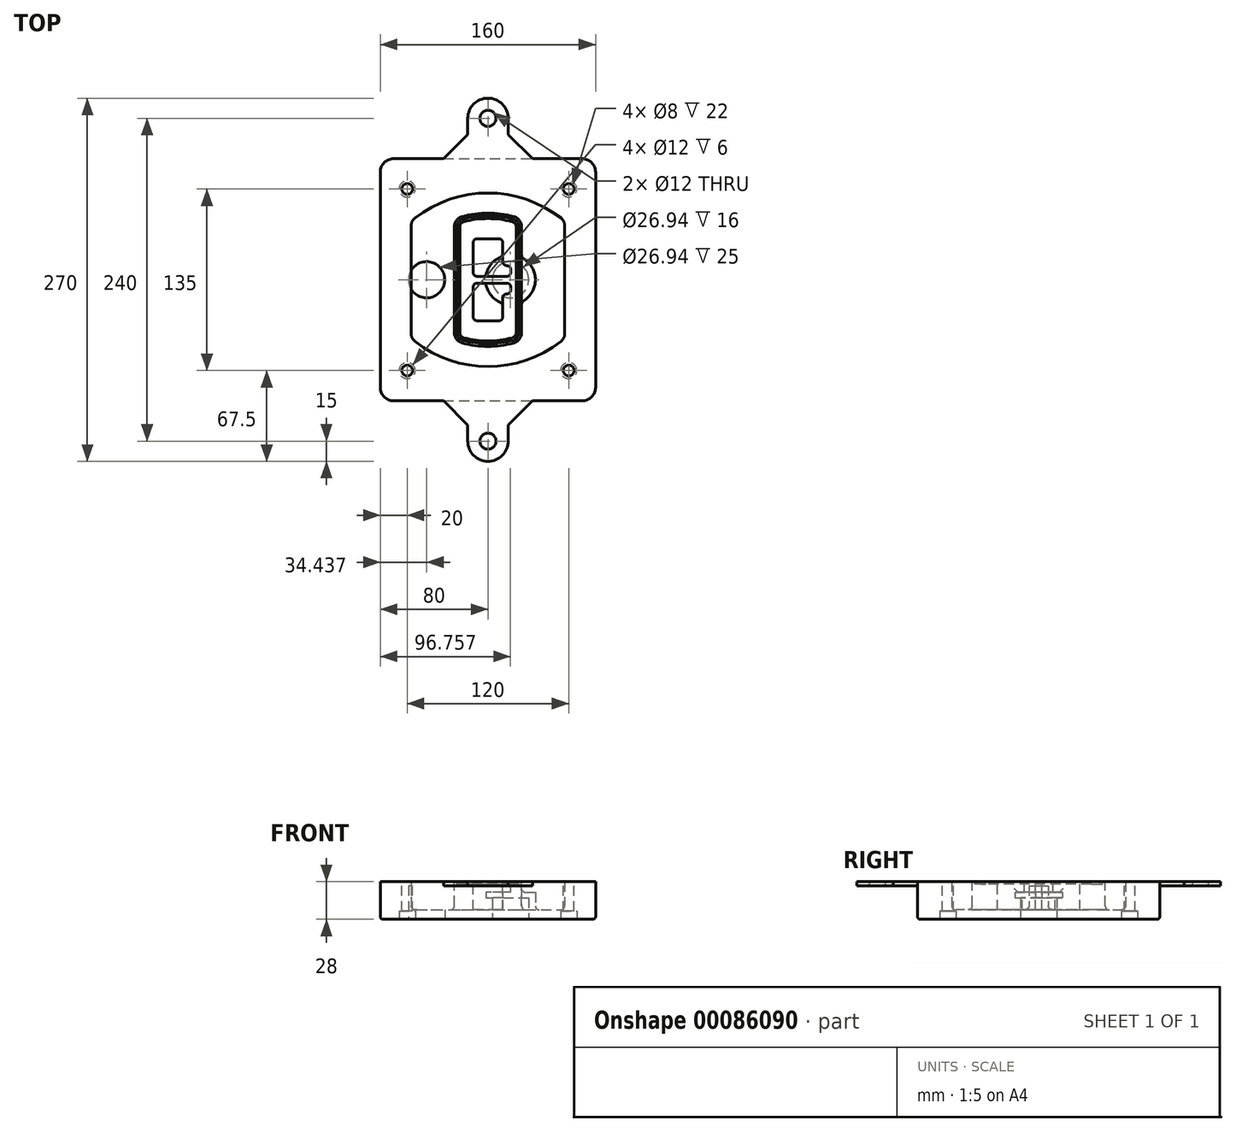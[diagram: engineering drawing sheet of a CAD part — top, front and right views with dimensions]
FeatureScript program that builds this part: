
annotation { "Feature Type Name" : "Feature", "Feature Type Description" : "" }
export const myFeature = defineFeature(function(context is Context, id is Id, definition is map)
    precondition{}
    {
        {
            var Q0;
            Q0=qCreatedBy(makeId("Top.planeOp"),FACE);
            var sketch = newSketch(context, id + "F0", { "sketchPlane" : qUnion([Q0])});
            skPoint(sketch, "E0.rect.middle", {"position": v(0, 0) * mm});
            skLineSegment(sketch, "E1.bottom", {"start": v(-70, -90) * mm, "end": v(70, -90) * mm});
            skLineSegment(sketch, "E1.top", {"start": v(-70, 90) * mm, "end": v(70, 90) * mm});
            skLineSegment(sketch, "E1.left", {"start": v(-80, -80) * mm, "end": v(-80, 80) * mm});
            skLineSegment(sketch, "E1.right", {"start": v(80, -80) * mm, "end": v(80, 80) * mm});
            skLineSegment(sketch, "E2", {"start": v(-80, 90) * mm, "end": v(80, -90) * mm, "construction": true});
            skLineSegment(sketch, "E3", {"start": v(80, 90) * mm, "end": v(-80, -90) * mm, "construction": true});
            skCircle(sketch, "E4", {"center": v(-60, 67.5) * mm, "radius": 4 * mm});
            skCircle(sketch, "E5", {"center": v(60, 67.5) * mm, "radius": 4 * mm});
            skCircle(sketch, "E6", {"center": v(60, -67.5) * mm, "radius": 4 * mm});
            skCircle(sketch, "E7", {"center": v(-60, -67.5) * mm, "radius": 4 * mm});
            skLineSegment(sketch, "E8", {"start": v(-60, 67.5) * mm, "end": v(60, 67.5) * mm, "construction": true});
            skLineSegment(sketch, "E9", {"start": v(60, 67.5) * mm, "end": v(60, -67.5) * mm, "construction": true});
            skLineSegment(sketch, "E10", {"start": v(60, -67.5) * mm, "end": v(-60, -67.5) * mm, "construction": true});
            skLineSegment(sketch, "E11", {"start": v(-60, -67.5) * mm, "end": v(-60, 67.5) * mm, "construction": true});
            skLineSegment(sketch, "E12", {"start": v(-60, 40.3) * mm, "end": v(-60, -40.3) * mm});
            skLineSegment(sketch, "E13", {"start": v(60, 40.3) * mm, "end": v(60, -40.3) * mm});
            skArc(sketch, "E14", {"start": v(56.15, 48.18) * mm, "mid": v(0, 67.5) * mm, "end": v(-56.15, 48.18) * mm});
            skArc(sketch, "E15", {"start": v(-56.15, -48.18) * mm, "mid": v(0, -67.5) * mm, "end": v(56.15, -48.18) * mm});
            skLineSegment(sketch, "E16", {"start": v(-60, 0) * mm, "end": v(60, 0) * mm, "construction": true});
            skPoint(sketch, "E17.visualSharp", {"position": v(-60, -45) * mm});
            skArc(sketch, "E17.filletArc", {"start": v(-60, -40.3) * mm, "mid": v(-58.99, -44.68) * mm, "end": v(-56.15, -48.18) * mm});
            skPoint(sketch, "E18.visualSharp", {"position": v(-60, 45) * mm});
            skArc(sketch, "E18.filletArc", {"start": v(-56.15, 48.18) * mm, "mid": v(-58.99, 44.68) * mm, "end": v(-60, 40.3) * mm});
            skPoint(sketch, "E19.visualSharp", {"position": v(60, 45) * mm});
            skArc(sketch, "E19.filletArc", {"start": v(60, 40.3) * mm, "mid": v(58.99, 44.68) * mm, "end": v(56.15, 48.18) * mm});
            skPoint(sketch, "E20.visualSharp", {"position": v(60, -45) * mm});
            skArc(sketch, "E20.filletArc", {"start": v(56.15, -48.18) * mm, "mid": v(58.99, -44.68) * mm, "end": v(60, -40.3) * mm});
            skPoint(sketch, "E21.visualSharp", {"position": v(-80, 90) * mm});
            skArc(sketch, "E21.filletArc", {"start": v(-70, 90) * mm, "mid": v(-77.07, 87.07) * mm, "end": v(-80, 80) * mm});
            skPoint(sketch, "E22.visualSharp", {"position": v(80, 90) * mm});
            skArc(sketch, "E22.filletArc", {"start": v(80, 80) * mm, "mid": v(77.07, 87.07) * mm, "end": v(70, 90) * mm});
            skPoint(sketch, "E23.visualSharp", {"position": v(80, -90) * mm});
            skArc(sketch, "E23.filletArc", {"start": v(70, -90) * mm, "mid": v(77.07, -87.07) * mm, "end": v(80, -80) * mm});
            skPoint(sketch, "E24.visualSharp", {"position": v(-80, -90) * mm});
            skArc(sketch, "E24.filletArc", {"start": v(-80, -80) * mm, "mid": v(-77.07, -87.07) * mm, "end": v(-70, -90) * mm});
            skArc(sketch, "E25.0", {"start": v(57, 40.3) * mm, "mid": v(56.3, 43.36) * mm, "end": v(54.3, 45.81) * mm});
            skLineSegment(sketch, "E25.1", {"start": v(57, 40.3) * mm, "end": v(57, -40.3) * mm});
            skArc(sketch, "E25.2", {"start": v(54.3, -45.81) * mm, "mid": v(56.3, -43.36) * mm, "end": v(57, -40.3) * mm});
            skArc(sketch, "E25.3", {"start": v(-54.3, -45.81) * mm, "mid": v(0, -64.5) * mm, "end": v(54.3, -45.81) * mm});
            skArc(sketch, "E25.4", {"start": v(-57, -40.3) * mm, "mid": v(-56.3, -43.36) * mm, "end": v(-54.3, -45.81) * mm});
            skArc(sketch, "E25.5", {"start": v(54.3, 45.81) * mm, "mid": v(0, 64.5) * mm, "end": v(-54.3, 45.81) * mm});
            skLineSegment(sketch, "E25.6", {"start": v(-57, 40.3) * mm, "end": v(-57, -40.3) * mm});
            skArc(sketch, "E25.7", {"start": v(-54.3, 45.81) * mm, "mid": v(-56.3, 43.36) * mm, "end": v(-57, 40.3) * mm});
            skArc(sketch, "E26.0", {"start": v(-58.62, 51.33) * mm, "mid": v(-62.58, 46.43) * mm, "end": v(-64, 40.3) * mm});
            skArc(sketch, "E26.1", {"start": v(58.62, 51.33) * mm, "mid": v(0, 71.5) * mm, "end": v(-58.62, 51.33) * mm});
            skArc(sketch, "E26.2", {"start": v(64, 40.3) * mm, "mid": v(62.58, 46.43) * mm, "end": v(58.62, 51.33) * mm});
            skLineSegment(sketch, "E26.3", {"start": v(64, 40.3) * mm, "end": v(64, -40.3) * mm});
            skArc(sketch, "E26.4", {"start": v(58.62, -51.33) * mm, "mid": v(62.58, -46.43) * mm, "end": v(64, -40.3) * mm});
            skLineSegment(sketch, "E26.5", {"start": v(-64, 40.3) * mm, "end": v(-64, -40.3) * mm});
            skArc(sketch, "E26.6", {"start": v(-58.62, -51.33) * mm, "mid": v(0, -71.5) * mm, "end": v(58.62, -51.33) * mm});
            skArc(sketch, "E26.7", {"start": v(-64, -40.3) * mm, "mid": v(-62.58, -46.43) * mm, "end": v(-58.62, -51.33) * mm});
            skSolve(sketch);
        }
        {
            var Q0;
            Q0=makeQuery(id+"F0.imprint","IMPRINT",FACE,{"disambiguationData":[TD([[makeQuery(id+"F0.imprint","IMPRINT",EDGE,{"derivedFrom":sQuery(id+"F0.wireOp",EDGE,"E1.bottom")}),1.0]])]});
            var Q1;
            Q1=makeQuery(id+"F0.imprint","IMPRINT",FACE,{"disambiguationData":[TD([[makeQuery(id+"F0.imprint","IMPRINT",EDGE,{"derivedFrom":sQuery(id+"F0.wireOp",EDGE,"E12")}),1.0]])]});
            var Q2;
            Q2=makeQuery(id+"F0.imprint","IMPRINT",FACE,{"disambiguationData":[TD([[makeQuery(id+"F0.imprint","IMPRINT",EDGE,{"derivedFrom":sQuery(id+"F0.wireOp",EDGE,"E25.0")}),1.0]])]});
            var Q3;
            Q3=makeQuery(id+"F0.imprint","IMPRINT",FACE,{"disambiguationData":[TD([[makeQuery(id+"F0.imprint","IMPRINT",EDGE,{"derivedFrom":sQuery(id+"F0.wireOp",EDGE,"E12")}),-1.0]])]});
            extrude(context, id + "F1", {"entities" : qUnion([Q0, Q1, Q2, Q3]), "oppositeDirection" : true, "depth" : 25 * mm});
        }
        {
            var Q0;
            Q0=makeQuery(id+"F0.imprint","IMPRINT",FACE,{"disambiguationData":[TD([[makeQuery(id+"F0.imprint","IMPRINT",EDGE,{"derivedFrom":sQuery(id+"F0.wireOp",EDGE,"E12")}),1.0]])]});
            extrude(context, id + "F2", {"entities" : qUnion([Q0]), "operationType" : NewBodyOperationType.ADD, "depth" : 3 * mm});
        }
        {
            var Q0;
            Q0=makeQuery(id+"F0.imprint","IMPRINT",FACE,{"disambiguationData":[TD([[makeQuery(id+"F0.imprint","IMPRINT",EDGE,{"derivedFrom":sQuery(id+"F0.wireOp",EDGE,"E25.0")}),1.0]])]});
            extrude(context, id + "F3", {"entities" : qUnion([Q0]), "operationType" : NewBodyOperationType.REMOVE, "oppositeDirection" : true, "depth" : 18 * mm});
        }
        {
            var Q0;
            Q0=makeQuery(id+"F2.opExtrude","CAP_FACE",FACE,{"disambiguationData":[OSD([sQuery(id+"F0.wireOp",EDGE,"E12"),sQuery(id+"F0.wireOp",EDGE,"E13"),sQuery(id+"F0.wireOp",EDGE,"E14"),sQuery(id+"F0.wireOp",EDGE,"E15"),sQuery(id+"F0.wireOp",EDGE,"E17.filletArc"),sQuery(id+"F0.wireOp",EDGE,"E18.filletArc"),sQuery(id+"F0.wireOp",EDGE,"E19.filletArc"),sQuery(id+"F0.wireOp",EDGE,"E20.filletArc"),sQuery(id+"F0.wireOp",EDGE,"E25.0"),sQuery(id+"F0.wireOp",EDGE,"E25.1"),sQuery(id+"F0.wireOp",EDGE,"E25.2"),sQuery(id+"F0.wireOp",EDGE,"E25.3"),sQuery(id+"F0.wireOp",EDGE,"E25.4"),sQuery(id+"F0.wireOp",EDGE,"E25.5"),sQuery(id+"F0.wireOp",EDGE,"E25.6"),sQuery(id+"F0.wireOp",EDGE,"E25.7")])],"isStart":false});
            var sketch = newSketch(context, id + "F4", { "sketchPlane" : qUnion([Q0])});
            skArc(sketch, "E27.0", {"start": v(-19.08, -46.97) * mm, "mid": v(0, -49.5) * mm, "end": v(19.08, -46.97) * mm});
            skArc(sketch, "E28.0", {"start": v(19.08, 46.97) * mm, "mid": v(0, 49.5) * mm, "end": v(-19.08, 46.97) * mm});
            skLineSegment(sketch, "E29", {"start": v(-25, 39.25) * mm, "end": v(-25, -39.25) * mm});
            skLineSegment(sketch, "E30", {"start": v(25, 39.25) * mm, "end": v(25, -39.25) * mm});
            skLineSegment(sketch, "E31", {"start": v(-25, 45.1) * mm, "end": v(25, 45.1) * mm, "construction": true});
            skLineSegment(sketch, "E32", {"start": v(-25, -45.1) * mm, "end": v(25, -45.1) * mm, "construction": true});
            skPoint(sketch, "E33.visualSharp", {"position": v(-25, 45.1) * mm});
            skArc(sketch, "E33.filletArc", {"start": v(-19.08, 46.97) * mm, "mid": v(-23.35, 44.11) * mm, "end": v(-25, 39.25) * mm});
            skPoint(sketch, "E34.visualSharp", {"position": v(25, 45.1) * mm});
            skArc(sketch, "E34.filletArc", {"start": v(25, 39.25) * mm, "mid": v(23.35, 44.11) * mm, "end": v(19.08, 46.97) * mm});
            skPoint(sketch, "E35.visualSharp", {"position": v(25, -45.1) * mm});
            skArc(sketch, "E35.filletArc", {"start": v(19.08, -46.97) * mm, "mid": v(23.35, -44.11) * mm, "end": v(25, -39.25) * mm});
            skPoint(sketch, "E36.visualSharp", {"position": v(-25, -45.1) * mm});
            skArc(sketch, "E36.filletArc", {"start": v(-25, -39.25) * mm, "mid": v(-23.35, -44.11) * mm, "end": v(-19.08, -46.97) * mm});
            skArc(sketch, "E37.0", {"start": v(54.3, 45.81) * mm, "mid": v(0, 64.5) * mm, "end": v(-54.3, 45.81) * mm});
            skArc(sketch, "E37.1", {"start": v(-54.3, 45.81) * mm, "mid": v(-56.3, 43.36) * mm, "end": v(-57, 40.3) * mm});
            skLineSegment(sketch, "E37.2", {"start": v(-57, 40.3) * mm, "end": v(-57, -40.3) * mm});
            skArc(sketch, "E37.3", {"start": v(-57, -40.3) * mm, "mid": v(-56.3, -43.36) * mm, "end": v(-54.3, -45.81) * mm});
            skArc(sketch, "E37.4", {"start": v(-54.3, -45.81) * mm, "mid": v(0, -64.5) * mm, "end": v(54.3, -45.81) * mm});
            skArc(sketch, "E37.5", {"start": v(54.3, -45.81) * mm, "mid": v(56.3, -43.36) * mm, "end": v(57, -40.3) * mm});
            skLineSegment(sketch, "E37.6", {"start": v(57, 40.3) * mm, "end": v(57, -40.3) * mm});
            skArc(sketch, "E37.7", {"start": v(57, 40.3) * mm, "mid": v(56.3, 43.36) * mm, "end": v(54.3, 45.81) * mm});
            skLineSegment(sketch, "E38.0", {"start": v(23, 39.25) * mm, "end": v(23, -39.25) * mm});
            skArc(sketch, "E38.1", {"start": v(18.56, -45.04) * mm, "mid": v(21.76, -42.9) * mm, "end": v(23, -39.25) * mm});
            skArc(sketch, "E38.2", {"start": v(-18.56, -45.04) * mm, "mid": v(0, -47.5) * mm, "end": v(18.56, -45.04) * mm});
            skArc(sketch, "E38.3", {"start": v(-23, -39.25) * mm, "mid": v(-21.76, -42.9) * mm, "end": v(-18.56, -45.04) * mm});
            skLineSegment(sketch, "E38.4", {"start": v(-23, 39.25) * mm, "end": v(-23, -39.25) * mm});
            skArc(sketch, "E38.5", {"start": v(23, 39.25) * mm, "mid": v(21.76, 42.9) * mm, "end": v(18.56, 45.04) * mm});
            skArc(sketch, "E38.6", {"start": v(-18.56, 45.04) * mm, "mid": v(-21.76, 42.9) * mm, "end": v(-23, 39.25) * mm});
            skArc(sketch, "E38.7", {"start": v(18.56, 45.04) * mm, "mid": v(0, 47.5) * mm, "end": v(-18.56, 45.04) * mm});
            skArc(sketch, "E39.0", {"start": v(21, 39.25) * mm, "mid": v(20.18, 41.68) * mm, "end": v(18.04, 43.1) * mm});
            skLineSegment(sketch, "E39.1", {"start": v(21, 39.25) * mm, "end": v(21, -39.25) * mm});
            skArc(sketch, "E39.2", {"start": v(18.04, -43.1) * mm, "mid": v(20.18, -41.68) * mm, "end": v(21, -39.25) * mm});
            skArc(sketch, "E39.3", {"start": v(-18.04, -43.1) * mm, "mid": v(0, -45.5) * mm, "end": v(18.04, -43.1) * mm});
            skArc(sketch, "E39.4", {"start": v(-21, -39.25) * mm, "mid": v(-20.18, -41.68) * mm, "end": v(-18.04, -43.1) * mm});
            skArc(sketch, "E39.5", {"start": v(18.04, 43.1) * mm, "mid": v(0, 45.5) * mm, "end": v(-18.04, 43.1) * mm});
            skLineSegment(sketch, "E39.6", {"start": v(-21, 39.25) * mm, "end": v(-21, -39.25) * mm});
            skArc(sketch, "E39.7", {"start": v(-18.04, 43.1) * mm, "mid": v(-20.18, 41.68) * mm, "end": v(-21, 39.25) * mm});
            skLineSegment(sketch, "E40", {"start": v(-25, 0) * mm, "end": v(25, 0) * mm, "construction": true});
            skLineSegment(sketch, "E41", {"start": v(-11, 5.5) * mm, "end": v(-11, 27.5) * mm});
            skLineSegment(sketch, "E42", {"start": v(-8, 30.5) * mm, "end": v(8, 30.5) * mm});
            skLineSegment(sketch, "E43", {"start": v(11, 27.5) * mm, "end": v(11, 13.5) * mm});
            skLineSegment(sketch, "E44", {"start": v(14, 10.5) * mm, "end": v(14, 10.5) * mm});
            skLineSegment(sketch, "E45", {"start": v(17, 7.5) * mm, "end": v(17, 5.5) * mm});
            skLineSegment(sketch, "E46", {"start": v(14, 2.5) * mm, "end": v(-8, 2.5) * mm});
            skPoint(sketch, "E47.visualSharp", {"position": v(-11, 30.5) * mm});
            skArc(sketch, "E47.filletArc", {"start": v(-8, 30.5) * mm, "mid": v(-10.12, 29.62) * mm, "end": v(-11, 27.5) * mm});
            skPoint(sketch, "E48.visualSharp", {"position": v(11, 30.5) * mm});
            skArc(sketch, "E48.filletArc", {"start": v(11, 27.5) * mm, "mid": v(10.12, 29.62) * mm, "end": v(8, 30.5) * mm});
            skPoint(sketch, "E49.visualSharp", {"position": v(11, 10.5) * mm});
            skArc(sketch, "E49.filletArc", {"start": v(11, 13.5) * mm, "mid": v(11.88, 11.38) * mm, "end": v(14, 10.5) * mm});
            skPoint(sketch, "E50.visualSharp", {"position": v(17, 10.5) * mm});
            skArc(sketch, "E50.filletArc", {"start": v(17, 7.5) * mm, "mid": v(16.12, 9.62) * mm, "end": v(14, 10.5) * mm});
            skPoint(sketch, "E51.visualSharp", {"position": v(17, 2.5) * mm});
            skArc(sketch, "E51.filletArc", {"start": v(14, 2.5) * mm, "mid": v(16.12, 3.38) * mm, "end": v(17, 5.5) * mm});
            skPoint(sketch, "E52.visualSharp", {"position": v(-11, 2.5) * mm});
            skArc(sketch, "E52.filletArc", {"start": v(-11, 5.5) * mm, "mid": v(-10.12, 3.38) * mm, "end": v(-8, 2.5) * mm});
            skLineSegment(sketch, "E53.0.MirrorCS", {"start": v(14, -2.5) * mm, "end": v(-8, -2.5) * mm});
            skArc(sketch, "E54.0.MirrorCS", {"start": v(-11, -5.5) * mm, "mid": v(-10.12, -3.38) * mm, "end": v(-8, -2.5) * mm});
            skLineSegment(sketch, "E55.0.MirrorCS", {"start": v(-11, -5.5) * mm, "end": v(-11, -27.5) * mm});
            skArc(sketch, "E56.0.MirrorCS", {"start": v(-8, -30.5) * mm, "mid": v(-10.12, -29.62) * mm, "end": v(-11, -27.5) * mm});
            skLineSegment(sketch, "E57.0.MirrorCS", {"start": v(-8, -30.5) * mm, "end": v(8, -30.5) * mm});
            skArc(sketch, "E58.0.MirrorCS", {"start": v(11, -27.5) * mm, "mid": v(10.12, -29.62) * mm, "end": v(8, -30.5) * mm});
            skLineSegment(sketch, "E59.0.MirrorCS", {"start": v(11, -27.5) * mm, "end": v(11, -13.5) * mm});
            skArc(sketch, "E60.0.MirrorCS", {"start": v(11, -13.5) * mm, "mid": v(11.88, -11.38) * mm, "end": v(14, -10.5) * mm});
            skArc(sketch, "E61.0.MirrorCS", {"start": v(17, -7.5) * mm, "mid": v(16.12, -9.62) * mm, "end": v(14, -10.5) * mm});
            skLineSegment(sketch, "E62.0.MirrorCS", {"start": v(17, -7.5) * mm, "end": v(17, -5.5) * mm});
            skArc(sketch, "E63.0.MirrorCS", {"start": v(14, -2.5) * mm, "mid": v(16.12, -3.38) * mm, "end": v(17, -5.5) * mm});
            skSolve(sketch);
        }
        {
            var Q0;
            Q0=makeQuery(id+"F4.imprint","IMPRINT",FACE,{"disambiguationData":[TD([[makeQuery(id+"F4.imprint","IMPRINT",EDGE,{"derivedFrom":sQuery(id+"F4.wireOp",EDGE,"E27.0")}),1.0]])]});
            var Q1;
            Q1=makeQuery(id+"F4.imprint","IMPRINT",FACE,{"disambiguationData":[TD([[makeQuery(id+"F4.imprint","IMPRINT",EDGE,{"derivedFrom":sQuery(id+"F4.wireOp",EDGE,"E38.0")}),-1.0]])]});
            var Q2;
            Q2=makeQuery(id+"F4.imprint","IMPRINT",FACE,{"disambiguationData":[TD([[makeQuery(id+"F4.imprint","IMPRINT",EDGE,{"derivedFrom":sQuery(id+"F4.wireOp",EDGE,"E39.0")}),1.0]])]});
            extrude(context, id + "F5", {"entities" : qUnion([Q0, Q1, Q2]), "operationType" : NewBodyOperationType.ADD, "endBound" : BoundingType.UP_TO_NEXT, "oppositeDirection" : true, "depth" : 25 * mm});
        }
        {
            var Q0;
            Q0=makeQuery(id+"F4.imprint","IMPRINT",FACE,{"disambiguationData":[TD([[makeQuery(id+"F4.imprint","IMPRINT",EDGE,{"derivedFrom":sQuery(id+"F4.wireOp",EDGE,"E38.0")}),-1.0]])]});
            extrude(context, id + "F6", {"entities" : qUnion([Q0]), "operationType" : NewBodyOperationType.REMOVE, "oppositeDirection" : true, "depth" : 2 * mm});
        }
        {
            var Q0;
            Q0=makeQuery(id+"F1.opExtrude","CAP_FACE",FACE,{"disambiguationData":[OSD([sQuery(id+"F0.wireOp",EDGE,"E1.bottom"),sQuery(id+"F0.wireOp",EDGE,"E1.top"),sQuery(id+"F0.wireOp",EDGE,"E1.left"),sQuery(id+"F0.wireOp",EDGE,"E1.right"),sQuery(id+"F0.wireOp",EDGE,"E4"),sQuery(id+"F0.wireOp",EDGE,"E5"),sQuery(id+"F0.wireOp",EDGE,"E6"),sQuery(id+"F0.wireOp",EDGE,"E7"),sQuery(id+"F0.wireOp",EDGE,"E21.filletArc"),sQuery(id+"F0.wireOp",EDGE,"E22.filletArc"),sQuery(id+"F0.wireOp",EDGE,"E23.filletArc"),sQuery(id+"F0.wireOp",EDGE,"E24.filletArc")])],"isStart":false});
            var sketch = newSketch(context, id + "F7", { "sketchPlane" : qUnion([Q0])});
            skCircle(sketch, "E64", {"center": v(16.76, 0) * mm, "radius": 13.47 * mm});
            skCircle(sketch, "E65", {"center": v(-45.56, 0) * mm, "radius": 13.47 * mm});
            skLineSegment(sketch, "E66", {"start": v(80, 0) * mm, "end": v(-80, 0) * mm});
            skCircle(sketch, "E67", {"center": v(16.76, 0) * mm, "radius": 18.47 * mm});
            skCircle(sketch, "E68", {"center": v(60, -67.5) * mm, "radius": 6 * mm});
            skCircle(sketch, "E69", {"center": v(-60, -67.5) * mm, "radius": 6 * mm});
            skCircle(sketch, "E70", {"center": v(-60, 67.5) * mm, "radius": 6 * mm});
            skCircle(sketch, "E71", {"center": v(60, 67.5) * mm, "radius": 6 * mm});
            skSolve(sketch);
        }
        {
            var Q0;
            {var subQ1=sQuery(id+"F7.wireOp",EDGE,"E66");var subQ4=sQuery(id+"F7.wireOp",EDGE,"E64");var subQ6=makeQuery(id+"F7.imprint","INTERSECT",VERTEX,{"disambiguationData":[OD(0.0)],"derivedFrom":[subQ4,subQ1]});Q0=makeQuery(id+"F7.imprint","IMPRINT",FACE,{"disambiguationData":[TD([[makeQuery(id+"F7.imprint","IMPRINT",EDGE,{"disambiguationData":[TD([[subQ6,-1.0]])],"derivedFrom":subQ4}),-1.0]])]});}
            var Q1;
            {var subQ0=sQuery(id+"F7.wireOp",EDGE,"E66");var subQ1=sQuery(id+"F7.wireOp",EDGE,"E64");var subQ3=makeQuery(id+"F7.imprint","INTERSECT",VERTEX,{"disambiguationData":[OD(0.0)],"derivedFrom":[subQ1,subQ0]});Q1=makeQuery(id+"F7.imprint","IMPRINT",FACE,{"disambiguationData":[TD([[makeQuery(id+"F7.imprint","IMPRINT",EDGE,{"disambiguationData":[TD([[subQ3,-1.0]])],"derivedFrom":subQ1}),1.0]])]});}
            var Q2;
            {var subQ0=sQuery(id+"F7.wireOp",EDGE,"E66");var subQ1=sQuery(id+"F7.wireOp",EDGE,"E64");var subQ3=makeQuery(id+"F7.imprint","INTERSECT",VERTEX,{"disambiguationData":[OD(0.0)],"derivedFrom":[subQ1,subQ0]});Q2=makeQuery(id+"F7.imprint","IMPRINT",FACE,{"disambiguationData":[TD([[makeQuery(id+"F7.imprint","IMPRINT",EDGE,{"disambiguationData":[TD([[subQ3,1.0]])],"derivedFrom":subQ1}),1.0]])]});}
            var Q3;
            {var subQ1=sQuery(id+"F7.wireOp",EDGE,"E66");var subQ4=sQuery(id+"F7.wireOp",EDGE,"E64");var subQ6=makeQuery(id+"F7.imprint","INTERSECT",VERTEX,{"disambiguationData":[OD(0.0)],"derivedFrom":[subQ4,subQ1]});Q3=makeQuery(id+"F7.imprint","IMPRINT",FACE,{"disambiguationData":[TD([[makeQuery(id+"F7.imprint","IMPRINT",EDGE,{"disambiguationData":[TD([[subQ6,1.0]])],"derivedFrom":subQ4}),-1.0]])]});}
            extrude(context, id + "F8", {"entities" : qUnion([Q0, Q1, Q2, Q3]), "operationType" : NewBodyOperationType.ADD, "oppositeDirection" : true, "depth" : 20 * mm});
        }
        {
            var Q0;
            {var subQ0=sQuery(id+"F7.wireOp",EDGE,"E66");var subQ1=sQuery(id+"F7.wireOp",EDGE,"E64");var subQ3=makeQuery(id+"F7.imprint","INTERSECT",VERTEX,{"disambiguationData":[OD(0.0)],"derivedFrom":[subQ1,subQ0]});Q0=makeQuery(id+"F7.imprint","IMPRINT",FACE,{"disambiguationData":[TD([[makeQuery(id+"F7.imprint","IMPRINT",EDGE,{"disambiguationData":[TD([[subQ3,-1.0]])],"derivedFrom":subQ1}),1.0]])]});}
            var Q1;
            {var subQ0=sQuery(id+"F7.wireOp",EDGE,"E66");var subQ1=sQuery(id+"F7.wireOp",EDGE,"E64");var subQ3=makeQuery(id+"F7.imprint","INTERSECT",VERTEX,{"disambiguationData":[OD(0.0)],"derivedFrom":[subQ1,subQ0]});Q1=makeQuery(id+"F7.imprint","IMPRINT",FACE,{"disambiguationData":[TD([[makeQuery(id+"F7.imprint","IMPRINT",EDGE,{"disambiguationData":[TD([[subQ3,1.0]])],"derivedFrom":subQ1}),1.0]])]});}
            extrude(context, id + "F9", {"entities" : qUnion([Q0, Q1]), "operationType" : NewBodyOperationType.REMOVE, "oppositeDirection" : true, "depth" : 16 * mm});
        }
        {
            var Q0;
            {var subQ0=sQuery(id+"F7.wireOp",EDGE,"E66");var subQ1=sQuery(id+"F7.wireOp",EDGE,"E65");var subQ3=makeQuery(id+"F7.imprint","INTERSECT",VERTEX,{"disambiguationData":[OD(0.0)],"derivedFrom":[subQ1,subQ0]});Q0=makeQuery(id+"F7.imprint","IMPRINT",FACE,{"disambiguationData":[TD([[makeQuery(id+"F7.imprint","IMPRINT",EDGE,{"disambiguationData":[TD([[subQ3,-1.0]])],"derivedFrom":subQ1}),1.0]])]});}
            var Q1;
            {var subQ0=sQuery(id+"F7.wireOp",EDGE,"E66");var subQ1=sQuery(id+"F7.wireOp",EDGE,"E65");var subQ3=makeQuery(id+"F7.imprint","INTERSECT",VERTEX,{"disambiguationData":[OD(0.0)],"derivedFrom":[subQ1,subQ0]});Q1=makeQuery(id+"F7.imprint","IMPRINT",FACE,{"disambiguationData":[TD([[makeQuery(id+"F7.imprint","IMPRINT",EDGE,{"disambiguationData":[TD([[subQ3,1.0]])],"derivedFrom":subQ1}),1.0]])]});}
            extrude(context, id + "F10", {"entities" : qUnion([Q0, Q1]), "operationType" : NewBodyOperationType.REMOVE, "oppositeDirection" : true, "depth" : 25 * mm});
        }
        {
            var Q0;
            Q0=makeQuery(id+"F7.imprint","IMPRINT",FACE,{"disambiguationData":[TD([[makeQuery(id+"F7.imprint","IMPRINT",EDGE,{"derivedFrom":sQuery(id+"F7.wireOp",EDGE,"E68")}),1.0]])]});
            var Q1;
            Q1=makeQuery(id+"F7.imprint","IMPRINT",FACE,{"disambiguationData":[TD([[makeQuery(id+"F7.imprint","IMPRINT",EDGE,{"derivedFrom":makeQuery(id+"F1.opExtrude","CAP_EDGE",EDGE,{"disambiguationData":[OSD([sQuery(id+"F0.wireOp",EDGE,"E5")])],"isStart":false})}),-1.0]])]});
            var Q2;
            Q2=makeQuery(id+"F7.imprint","IMPRINT",FACE,{"disambiguationData":[TD([[makeQuery(id+"F7.imprint","IMPRINT",EDGE,{"derivedFrom":sQuery(id+"F7.wireOp",EDGE,"E69")}),1.0]])]});
            var Q3;
            Q3=makeQuery(id+"F7.imprint","IMPRINT",FACE,{"disambiguationData":[TD([[makeQuery(id+"F7.imprint","IMPRINT",EDGE,{"derivedFrom":makeQuery(id+"F1.opExtrude","CAP_EDGE",EDGE,{"disambiguationData":[OSD([sQuery(id+"F0.wireOp",EDGE,"E4")])],"isStart":false})}),-1.0]])]});
            var Q4;
            Q4=makeQuery(id+"F7.imprint","IMPRINT",FACE,{"disambiguationData":[TD([[makeQuery(id+"F7.imprint","IMPRINT",EDGE,{"derivedFrom":sQuery(id+"F7.wireOp",EDGE,"E70")}),1.0]])]});
            var Q5;
            Q5=makeQuery(id+"F7.imprint","IMPRINT",FACE,{"disambiguationData":[TD([[makeQuery(id+"F7.imprint","IMPRINT",EDGE,{"derivedFrom":makeQuery(id+"F1.opExtrude","CAP_EDGE",EDGE,{"disambiguationData":[OSD([sQuery(id+"F0.wireOp",EDGE,"E7")])],"isStart":false})}),-1.0]])]});
            var Q6;
            Q6=makeQuery(id+"F7.imprint","IMPRINT",FACE,{"disambiguationData":[TD([[makeQuery(id+"F7.imprint","IMPRINT",EDGE,{"derivedFrom":sQuery(id+"F7.wireOp",EDGE,"E71")}),1.0]])]});
            var Q7;
            Q7=makeQuery(id+"F7.imprint","IMPRINT",FACE,{"disambiguationData":[TD([[makeQuery(id+"F7.imprint","IMPRINT",EDGE,{"derivedFrom":makeQuery(id+"F1.opExtrude","CAP_EDGE",EDGE,{"disambiguationData":[OSD([sQuery(id+"F0.wireOp",EDGE,"E6")])],"isStart":false})}),-1.0]])]});
            extrude(context, id + "F11", {"entities" : qUnion([Q0, Q1, Q2, Q3, Q4, Q5, Q6, Q7]), "operationType" : NewBodyOperationType.REMOVE, "oppositeDirection" : true, "depth" : 6 * mm});
        }
        {
            var Q0;
            Q0=makeQuery(id+"F9.boolean.opBoolean","COPY",FACE,{"derivedFrom":makeQuery(id+"F9.opExtrude","CAP_FACE",FACE,{"disambiguationData":[OSD([sQuery(id+"F7.wireOp",EDGE,"E64")])],"isStart":false})});
            var sketch = newSketch(context, id + "F12", { "sketchPlane" : qUnion([Q0])});
            skArc(sketch, "E72.0", {"start": v(11, 17.55) * mm, "mid": v(2.57, 11.82) * mm, "end": v(-1.54, 2.5) * mm});
            skArc(sketch, "E72.1", {"start": v(-1.54, -2.5) * mm, "mid": v(2.57, -11.82) * mm, "end": v(11, -17.55) * mm});
            skLineSegment(sketch, "E73", {"start": v(-1.54, -2.5) * mm, "end": v(14, -2.5) * mm});
            skLineSegment(sketch, "E74.0", {"start": v(14, 2.5) * mm, "end": v(-1.54, 2.5) * mm});
            skArc(sketch, "E74.1", {"start": v(14, 2.5) * mm, "mid": v(16.12, 3.38) * mm, "end": v(17, 5.5) * mm});
            skLineSegment(sketch, "E74.2", {"start": v(17, 7.5) * mm, "end": v(17, 5.5) * mm});
            skArc(sketch, "E74.3", {"start": v(17, 7.5) * mm, "mid": v(16.12, 9.62) * mm, "end": v(14, 10.5) * mm});
            skArc(sketch, "E74.4", {"start": v(11, 13.5) * mm, "mid": v(11.88, 11.38) * mm, "end": v(14, 10.5) * mm});
            skLineSegment(sketch, "E74.5", {"start": v(11, 17.55) * mm, "end": v(11, 13.5) * mm});
            skLineSegment(sketch, "E74.7", {"start": v(14, -2.5) * mm, "end": v(-1.54, -2.5) * mm});
            skArc(sketch, "E74.8", {"start": v(14, -2.5) * mm, "mid": v(16.12, -3.38) * mm, "end": v(17, -5.5) * mm});
            skLineSegment(sketch, "E74.9", {"start": v(17, -7.5) * mm, "end": v(17, -5.5) * mm});
            skArc(sketch, "E74.10", {"start": v(17, -7.5) * mm, "mid": v(16.12, -9.62) * mm, "end": v(14, -10.5) * mm});
            skArc(sketch, "E74.11", {"start": v(11, -13.5) * mm, "mid": v(11.88, -11.38) * mm, "end": v(14, -10.5) * mm});
            skLineSegment(sketch, "E74.12", {"start": v(11, -17.55) * mm, "end": v(11, -13.5) * mm});
            skPoint(sketch, "E75.orphan", {"position": v(11, -27.5) * mm});
            skPoint(sketch, "E76.orphan", {"position": v(-8, -2.5) * mm});
            skPoint(sketch, "E77.orphan", {"position": v(-8, 2.5) * mm});
            skPoint(sketch, "E78.orphan", {"position": v(11, 27.5) * mm});
            skSolve(sketch);
        }
        {
            var Q0;
            {var subQ7=sQuery(id+"F12.wireOp",EDGE,"E72.0");var subQ14=sQuery(id+"F12.wireOp",EDGE,"E72.1");var subQ16=sQuery(id+"F12.wireOp",EDGE,"E74.1");var subQ18=sQuery(id+"F12.wireOp",EDGE,"E74.8");Q0=qUnion([makeQuery(id+"F12.imprint","IMPRINT",FACE,{"disambiguationData":[TD([[makeQuery(id+"F12.imprint","IMPRINT",EDGE,{"derivedFrom":subQ7}),1.0]])]}),makeQuery(id+"F12.imprint","IMPRINT",FACE,{"disambiguationData":[TD([[makeQuery(id+"F12.imprint","IMPRINT",EDGE,{"derivedFrom":subQ14}),1.0]])]}),makeQuery(id+"F12.imprint","IMPRINT",FACE,{"disambiguationData":[TD([[makeQuery(id+"F12.imprint","IMPRINT",EDGE,{"derivedFrom":subQ16}),1.0]])]}),makeQuery(id+"F12.imprint","IMPRINT",FACE,{"disambiguationData":[TD([[makeQuery(id+"F12.imprint","IMPRINT",EDGE,{"derivedFrom":subQ18}),-1.0]])]})]);}
            var Q1;
            Q1=makeQuery(id+"F5.boolean.opBoolean","SPLIT",FACE,{"disambiguationData":[TD([makeQuery(id+"F5.opExtrude","SWEPT_FACE",FACE,{"disambiguationData":[OSD([sQuery(id+"F4.wireOp",EDGE,"E41")])]})])],"derivedFrom":makeQuery(id+"F3.boolean.opBoolean","COPY",FACE,{"derivedFrom":makeQuery(id+"F3.opExtrude","CAP_FACE",FACE,{"disambiguationData":[OSD([sQuery(id+"F0.wireOp",EDGE,"E25.0"),sQuery(id+"F0.wireOp",EDGE,"E25.1"),sQuery(id+"F0.wireOp",EDGE,"E25.2"),sQuery(id+"F0.wireOp",EDGE,"E25.3"),sQuery(id+"F0.wireOp",EDGE,"E25.4"),sQuery(id+"F0.wireOp",EDGE,"E25.5"),sQuery(id+"F0.wireOp",EDGE,"E25.6"),sQuery(id+"F0.wireOp",EDGE,"E25.7")])],"isStart":false})})});
            extrude(context, id + "F13", {"entities" : qUnion([Q0]), "operationType" : NewBodyOperationType.REMOVE, "endBound" : BoundingType.UP_TO_SURFACE, "endBoundEntityFace" : qUnion([Q1]), "depth" : 25 * mm});
        }
        {
            var Q0;
            Q0=makeQuery(id+"F3.boolean.opBoolean","COPY",EDGE,{"derivedFrom":makeQuery(id+"F3.opExtrude","CAP_EDGE",EDGE,{"disambiguationData":[OSD([sQuery(id+"F0.wireOp",EDGE,"E25.6")])],"isStart":false})});
            var Q1;
            Q1=makeQuery(id+"F8.boolean.opBoolean","INTERSECT",EDGE,{"derivedFrom":[makeQuery(id+"F5.opExtrude","SWEPT_FACE",FACE,{"disambiguationData":[OSD([sQuery(id+"F4.wireOp",EDGE,"E30")])]}),makeQuery(id+"F8.opExtrude","CAP_FACE",FACE,{"disambiguationData":[OSD([sQuery(id+"F7.wireOp",EDGE,"E67")])],"isStart":false})]});
            var Q2;
            Q2=makeQuery(id+"F8.boolean.opBoolean","INTERSECT",EDGE,{"disambiguationData":[OD(1.0)],"derivedFrom":[makeQuery(id+"F5.opExtrude","SWEPT_FACE",FACE,{"disambiguationData":[OSD([sQuery(id+"F4.wireOp",EDGE,"E30")])]}),makeQuery(id+"F8.opExtrude","SWEPT_FACE",FACE,{"disambiguationData":[OSD([sQuery(id+"F7.wireOp",EDGE,"E67")])]})]});
            var Q3;
            {var subQ0=sQuery(id+"F4.wireOp",EDGE,"E30");Q3=makeQuery(id+"F8.boolean.opBoolean","SPLIT",EDGE,{"disambiguationData":[TD([makeQuery(id+"F5.opExtrude","SWEPT_FACE",FACE,{"disambiguationData":[OSD([sQuery(id+"F4.wireOp",EDGE,"E35.filletArc")])]})])],"derivedFrom":makeQuery(id+"F5.opExtrude","CAP_EDGE",EDGE,{"disambiguationData":[OSD([subQ0])],"isStart":false})});}
            var Q4;
            {var subQ0=sQuery(id+"F0.wireOp",EDGE,"E25.7");var subQ1=sQuery(id+"F0.wireOp",EDGE,"E25.1");var subQ2=sQuery(id+"F0.wireOp",EDGE,"E25.6");var subQ3=sQuery(id+"F0.wireOp",EDGE,"E25.5");var subQ4=sQuery(id+"F0.wireOp",EDGE,"E25.4");var subQ5=sQuery(id+"F0.wireOp",EDGE,"E25.0");var subQ6=sQuery(id+"F0.wireOp",EDGE,"E25.2");var subQ7=sQuery(id+"F0.wireOp",EDGE,"E25.3");Q4=makeQuery(id+"F8.boolean.opBoolean","INTERSECT",EDGE,{"derivedFrom":[makeQuery(id+"F5.boolean.opBoolean","SPLIT",FACE,{"disambiguationData":[TD([makeQuery(id+"F2.opExtrude","SWEPT_FACE",FACE,{"disambiguationData":[OSD([subQ5])]})])],"derivedFrom":makeQuery(id+"F3.boolean.opBoolean","COPY",FACE,{"derivedFrom":makeQuery(id+"F3.opExtrude","CAP_FACE",FACE,{"disambiguationData":[OSD([subQ5,subQ1,subQ6,subQ7,subQ4,subQ3,subQ2,subQ0])],"isStart":false})})}),makeQuery(id+"F8.opExtrude","SWEPT_FACE",FACE,{"disambiguationData":[OSD([sQuery(id+"F7.wireOp",EDGE,"E67")])]})]});}
            var Q5;
            Q5=makeQuery(id+"F8.boolean.opBoolean","INTERSECT",EDGE,{"disambiguationData":[OD(0.0)],"derivedFrom":[makeQuery(id+"F5.opExtrude","SWEPT_FACE",FACE,{"disambiguationData":[OSD([sQuery(id+"F4.wireOp",EDGE,"E30")])]}),makeQuery(id+"F8.opExtrude","SWEPT_FACE",FACE,{"disambiguationData":[OSD([sQuery(id+"F7.wireOp",EDGE,"E67")])]})]});
            fillet(context, id + "F14", {"entities" : qUnion([Q0, Q1, Q2, Q3, Q4, Q5]), "radius" : 3 * mm, "tangentPropagation" : true, "allowEdgeOverflow" : false});
        }
        {
            var Q0;
            Q0=makeQuery(id+"F1.opExtrude","CAP_EDGE",EDGE,{"disambiguationData":[OSD([sQuery(id+"F0.wireOp",EDGE,"E1.bottom")])],"isStart":false});
            fillet(context, id + "F15", {"entities" : qUnion([Q0]), "radius" : 2 * mm, "tangentPropagation" : true, "allowEdgeOverflow" : false});
        }
        {
            var Q0;
            {var subQ0=sQuery(id+"F0.wireOp",EDGE,"E22.filletArc");var subQ1=sQuery(id+"F0.wireOp",EDGE,"E7");var subQ2=sQuery(id+"F0.wireOp",EDGE,"E6");var subQ3=sQuery(id+"F0.wireOp",EDGE,"E5");var subQ4=sQuery(id+"F0.wireOp",EDGE,"E4");var subQ5=sQuery(id+"F0.wireOp",EDGE,"E1.bottom");var subQ6=sQuery(id+"F0.wireOp",EDGE,"E21.filletArc");var subQ7=sQuery(id+"F0.wireOp",EDGE,"E1.top");var subQ8=sQuery(id+"F0.wireOp",EDGE,"E1.left");var subQ9=sQuery(id+"F0.wireOp",EDGE,"E1.right");var subQ10=sQuery(id+"F0.wireOp",EDGE,"E23.filletArc");var subQ11=sQuery(id+"F0.wireOp",EDGE,"E24.filletArc");Q0=makeQuery(id+"F2.boolean.opBoolean","SPLIT",FACE,{"disambiguationData":[TD([makeQuery(id+"F1.opExtrude","SWEPT_FACE",FACE,{"disambiguationData":[OSD([subQ5])]})])],"derivedFrom":makeQuery(id+"F1.opExtrude","CAP_FACE",FACE,{"disambiguationData":[OSD([subQ5,subQ7,subQ8,subQ9,subQ4,subQ3,subQ2,subQ1,subQ6,subQ0,subQ10,subQ11])],"isStart":true})});}
            var sketch = newSketch(context, id + "F16", { "sketchPlane" : qUnion([Q0])});
            skLineSegment(sketch, "E79", {"start": v(0, 90) * mm, "end": v(0, 120) * mm, "construction": true});
            skCircle(sketch, "E80", {"center": v(0, 120) * mm, "radius": 6 * mm});
            skArc(sketch, "E81", {"start": v(15, 120) * mm, "mid": v(0, 135) * mm, "end": v(-15, 120) * mm});
            skLineSegment(sketch, "E82", {"start": v(-15, 120) * mm, "end": v(-15, 108) * mm});
            skLineSegment(sketch, "E83", {"start": v(15, 120) * mm, "end": v(15, 108) * mm});
            skLineSegment(sketch, "E84", {"start": v(-15, 108) * mm, "end": v(-33, 90) * mm});
            skLineSegment(sketch, "E85", {"start": v(15, 108) * mm, "end": v(33, 90) * mm});
            skLineSegment(sketch, "E86", {"start": v(0, 0) * mm, "end": v(120.07, 0) * mm, "construction": true});
            skPoint(sketch, "E86.endSnap0", {"position": v(80, 0) * mm});
            skLineSegment(sketch, "E87.MirrorCS", {"start": v(15, -108) * mm, "end": v(33, -90) * mm});
            skCircle(sketch, "E88.MirrorC", {"center": v(0, -120) * mm, "radius": 6 * mm});
            skLineSegment(sketch, "E89.MirrorCS", {"start": v(-15, -108) * mm, "end": v(-33, -90) * mm});
            skLineSegment(sketch, "E90.MirrorCS", {"start": v(15, -120) * mm, "end": v(15, -108) * mm});
            skLineSegment(sketch, "E91.MirrorCS", {"start": v(-15, -120) * mm, "end": v(-15, -108) * mm});
            skArc(sketch, "E92.MirrorCS", {"start": v(15, -120) * mm, "mid": v(0, -135) * mm, "end": v(-15, -120) * mm});
            skSolve(sketch);
        }
        {
            var Q0;
            Q0=makeQuery(id+"F16.imprint","IMPRINT",FACE,{"disambiguationData":[TD([[makeQuery(id+"F16.imprint","IMPRINT",EDGE,{"derivedFrom":sQuery(id+"F16.wireOp",EDGE,"E80")}),-1.0]])]});
            var Q1;
            {var subQ1=sQuery(id+"F16.wireOp",EDGE,"E87.MirrorCS");Q1=makeQuery(id+"F16.imprint","IMPRINT",FACE,{"disambiguationData":[TD([[makeQuery(id+"F16.imprint","IMPRINT",EDGE,{"derivedFrom":subQ1}),1.0]])]});}
            var Q2;
            Q2=makeQuery(id+"F16.imprint","IMPRINT",FACE,{"disambiguationData":[TD([[makeQuery(id+"F16.imprint","IMPRINT",EDGE,{"derivedFrom":makeQuery(id+"F1.opExtrude","CAP_EDGE",EDGE,{"disambiguationData":[OSD([sQuery(id+"F0.wireOp",EDGE,"E1.left")])],"isStart":true})}),-1.0]])]});
            var Q3;
            Q3=makeQuery(id+"F2.opExtrude","CAP_FACE",FACE,{"disambiguationData":[OSD([sQuery(id+"F0.wireOp",EDGE,"E12"),sQuery(id+"F0.wireOp",EDGE,"E13"),sQuery(id+"F0.wireOp",EDGE,"E14"),sQuery(id+"F0.wireOp",EDGE,"E15"),sQuery(id+"F0.wireOp",EDGE,"E17.filletArc"),sQuery(id+"F0.wireOp",EDGE,"E18.filletArc"),sQuery(id+"F0.wireOp",EDGE,"E19.filletArc"),sQuery(id+"F0.wireOp",EDGE,"E20.filletArc"),sQuery(id+"F0.wireOp",EDGE,"E25.0"),sQuery(id+"F0.wireOp",EDGE,"E25.1"),sQuery(id+"F0.wireOp",EDGE,"E25.2"),sQuery(id+"F0.wireOp",EDGE,"E25.3"),sQuery(id+"F0.wireOp",EDGE,"E25.4"),sQuery(id+"F0.wireOp",EDGE,"E25.5"),sQuery(id+"F0.wireOp",EDGE,"E25.6"),sQuery(id+"F0.wireOp",EDGE,"E25.7")])],"isStart":false});
            extrude(context, id + "F17", {"entities" : qUnion([Q0, Q1, Q2]), "operationType" : NewBodyOperationType.ADD, "endBound" : BoundingType.UP_TO_SURFACE, "endBoundEntityFace" : qUnion([Q3]), "depth" : 25 * mm});
        }
    });
